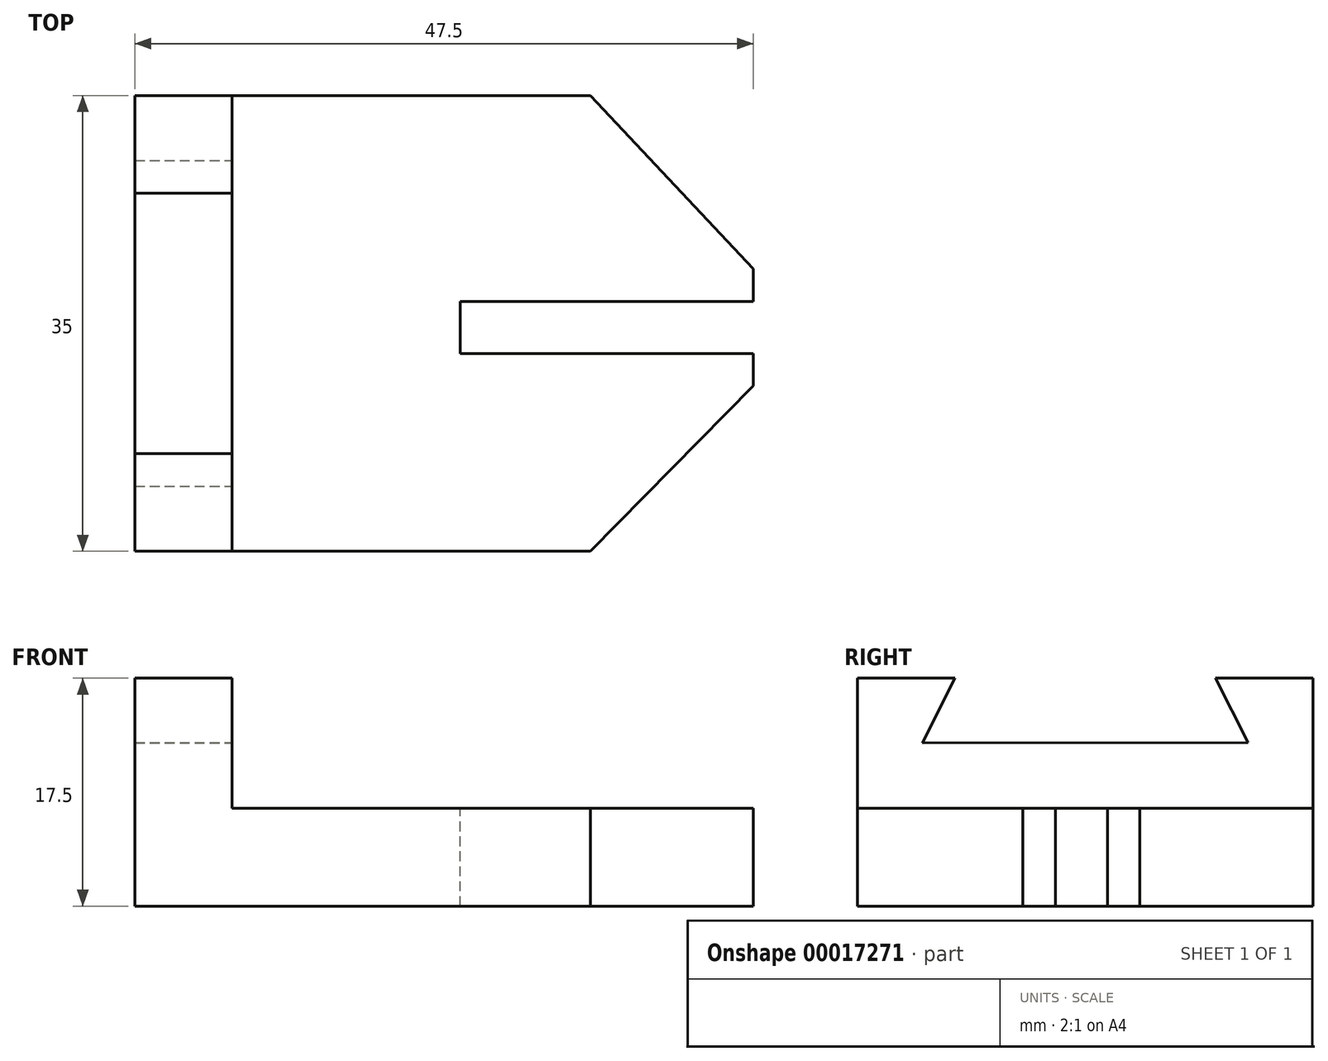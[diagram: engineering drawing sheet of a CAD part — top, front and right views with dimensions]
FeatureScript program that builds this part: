
annotation { "Feature Type Name" : "Feature", "Feature Type Description" : "" }
export const myFeature = defineFeature(function(context is Context, id is Id, definition is map)
    precondition{}
    {
        {
            var Q0;
            Q0=qCreatedBy(makeId("Front.planeOp"),FACE);
            var sketch = newSketch(context, id + "F0", { "sketchPlane" : qUnion([Q0])});
            skLineSegment(sketch, "E0", {"start": v(0, 0) * mm, "end": v(-19.53, 0) * mm});
            skLineSegment(sketch, "E1", {"start": v(-19.53, 0) * mm, "end": v(-19.53, 10) * mm});
            skLineSegment(sketch, "E2", {"start": v(-19.53, 10) * mm, "end": v(-27, 10) * mm});
            skLineSegment(sketch, "E3", {"start": v(-27, 10) * mm, "end": v(-27, -7.5) * mm});
            skLineSegment(sketch, "E4", {"start": v(-27, -7.5) * mm, "end": v(20.5, -7.5) * mm});
            skLineSegment(sketch, "E5", {"start": v(20.5, -7.5) * mm, "end": v(20.5, 0) * mm});
            skLineSegment(sketch, "E6", {"start": v(20.5, 0) * mm, "end": v(0, 0) * mm});
            skSolve(sketch);
        }
        {
            var Q0;
            Q0 = qSketchRegion(id + "F0", true);
            extrude(context, id + "F1", {"entities" : qUnion([Q0]), "depth" : 35 * mm});
        }
        {
            var Q0;
            Q0=makeQuery(id+"F1.opExtrude","SWEPT_FACE",FACE,{"disambiguationData":[OSD([sQuery(id+"F0.wireOp",EDGE,"E0"),sQuery(id+"F0.wireOp",EDGE,"E6")])]});
            var sketch = newSketch(context, id + "F2", { "sketchPlane" : qUnion([Q0])});
            skLineSegment(sketch, "E7", {"start": v(-2, -15.8) * mm, "end": v(20.5, -15.8) * mm});
            skLineSegment(sketch, "E8", {"start": v(-2, -15.8) * mm, "end": v(-2, -19.8) * mm});
            skLineSegment(sketch, "E9", {"start": v(-2, -19.8) * mm, "end": v(20.5, -19.8) * mm});
            skLineSegment(sketch, "E10", {"start": v(20.5, -19.8) * mm, "end": v(20.5, -15.8) * mm});
            skSolve(sketch);
        }
        {
            var Q0;
            Q0 = qSketchRegion(id + "F2", true);
            extrude(context, id + "F3", {"entities" : qUnion([Q0]), "operationType" : NewBodyOperationType.REMOVE, "endBound" : BoundingType.THROUGH_ALL, "oppositeDirection" : true, "depth" : 25 * mm});
        }
        {
            var Q0;
            Q0=makeQuery(id+"F1.opExtrude","SWEPT_FACE",FACE,{"disambiguationData":[OSD([sQuery(id+"F0.wireOp",EDGE,"E1")])]});
            var sketch = newSketch(context, id + "F4", { "sketchPlane" : qUnion([Q0])});
            skLineSegment(sketch, "E11", {"start": v(-30, 5.04) * mm, "end": v(-27.5, 10) * mm});
            skLineSegment(sketch, "E12", {"start": v(-5, 5.05) * mm, "end": v(-7.5, 10) * mm});
            skLineSegment(sketch, "E13", {"start": v(-7.5, 10) * mm, "end": v(-27.5, 10) * mm});
            skLineSegment(sketch, "E14", {"start": v(-30, 5.04) * mm, "end": v(-5, 5.05) * mm});
            skPoint(sketch, "E15", {"position": v(-27.5, 10) * mm});
            skPoint(sketch, "E16", {"position": v(-7.5, 10) * mm});
            skSolve(sketch);
        }
        {
            var Q0;
            Q0 = qSketchRegion(id + "F4", true);
            extrude(context, id + "F5", {"entities" : qUnion([Q0]), "operationType" : NewBodyOperationType.REMOVE, "endBound" : BoundingType.THROUGH_ALL, "oppositeDirection" : true, "depth" : 25 * mm});
        }
        {
            var Q0;
            Q0=makeQuery(id+"F1.opExtrude","SWEPT_FACE",FACE,{"disambiguationData":[OSD([sQuery(id+"F0.wireOp",EDGE,"E0"),sQuery(id+"F0.wireOp",EDGE,"E6")])]});
            var sketch = newSketch(context, id + "F6", { "sketchPlane" : qUnion([Q0])});
            skPoint(sketch, "E17", {"position": v(8, 0) * mm});
            skPoint(sketch, "E18", {"position": v(8, -35) * mm});
            skLineSegment(sketch, "E19", {"start": v(8, -35) * mm, "end": v(20.5, -22.3) * mm});
            skLineSegment(sketch, "E20", {"start": v(8, -35) * mm, "end": v(20.5, -35) * mm});
            skLineSegment(sketch, "E21", {"start": v(20.5, -35) * mm, "end": v(20.5, -22.3) * mm});
            skLineSegment(sketch, "E22", {"start": v(20.5, -13.3) * mm, "end": v(8, 0) * mm});
            skLineSegment(sketch, "E23", {"start": v(8, 0) * mm, "end": v(20.5, 0) * mm});
            skLineSegment(sketch, "E24", {"start": v(20.5, 0) * mm, "end": v(20.5, -13.3) * mm});
            skSolve(sketch);
        }
        {
            var Q0;
            Q0 = qSketchRegion(id + "F6", true);
            extrude(context, id + "F7", {"entities" : qUnion([Q0]), "operationType" : NewBodyOperationType.REMOVE, "endBound" : BoundingType.THROUGH_ALL, "oppositeDirection" : true, "depth" : 25 * mm});
        }
    });
